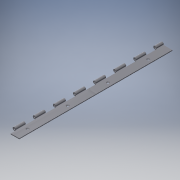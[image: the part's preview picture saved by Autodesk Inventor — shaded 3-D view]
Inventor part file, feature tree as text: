
AUTODESK INVENTOR PART (.ipt)
format: ipt  version: 2016 (Build 200138000, 138)  size: 190,464 bytes
history: native  units: mm
features: sketch x4, extrude x3, pattern_linear x1, hole x1
ambient origin geometry x8: Origin, YZ Plane, XZ Plane, XY Plane, X Axis, Y Axis, Z Axis, Center Point
bodies: Solid1 (feature_tree)
feature tree (9):
  extrude  "Extrusion1"  Depth=3.0mm
  extrude  "Extrusion2"  Depth=20.0mm
  pattern_linear  "Rectangular Pattern1"  Count1=180 Spacing1=0.0mm
  extrude  "Extrusion3"  Depth=80.0mm
  hole  "Hole1"  [1 undecoded]
  sketch  "Sketch2"  dims[d0=1.5mm d1=1.5mm d2=20.0mm d3=3.0mm d4=4.712389mm]
  sketch  "Sketch3"  dims[d5=304.8mm d6=0.0mm d8=20.0mm]
  sketch  "Sketch4"  dims[d9=6.0mm d10=1800.0mm d11=0.0mm]
  sketch  "Sketch5"  dims[d12=250.0mm d14=40.0mm d15=8.0mm d16=3.0mm d17=6.0mm d18=6.0mm d19=2.0mm d20=90.0deg d21=8.0mm d22=20.594885mm d24=30.0mm d25=10.0mm d26=6.0mm d27=10.0mm d28=0.0mm d29=40.0mm d30=80.0mm d31=80.0mm d32=80.0mm d33=80.0mm d34=80.0mm d35=80.0mm d36=80.0mm d37=80.0mm d38=80.0mm d39=80.0mm d40=80.0mm]
note: 1 required parameter value undecoded (feature->parameter linkage not recoverable at this tier; creation-order binding heuristic only, values carry confidence <= 0.55)
